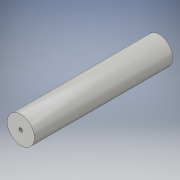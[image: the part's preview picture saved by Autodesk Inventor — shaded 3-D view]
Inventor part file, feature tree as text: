
AUTODESK INVENTOR PART (.ipt)
format: ipt  version: 2016 (Build 200138000, 138)  size: 113,152 bytes
history: native  units: in
note: dims shown in document units (in); Inventor stores cm internally (conversion verified against a paired STEP export)
features: sketch x3, extrude x2, hole x1, projected_geometry x1
ambient origin geometry x8: Origin, YZ Plane, XZ Plane, XY Plane, X Axis, Y Axis, Z Axis, Center Point
bodies: Solid1 (feature_tree)
feature tree (7):
  extrude  "Extrusion1"  Depth=3.8in TaperAngle=0.0deg
  extrude  "Extrusion2"  Depth=0.3in TaperAngle=0.0deg
  hole  "Hole1"  [1 undecoded]
  sketch  "Sketch1"  dims[d0=0.75in d1=3.8in d2=0.0in]
  sketch  "Sketch2"  dims[d3=0.1in d4=0.3in d5=0.0in]
  sketch  "Sketch3"  dims[d6=0.1in d7=0.75in d8=0.375in d9=0.25in d10=0.5635in d11=1.0in d12=0.8108in]
  projected_geometry  "Projected Loop1"
note: 1 required parameter value undecoded (feature->parameter linkage not recoverable at this tier; creation-order binding heuristic only, values carry confidence <= 0.55)
